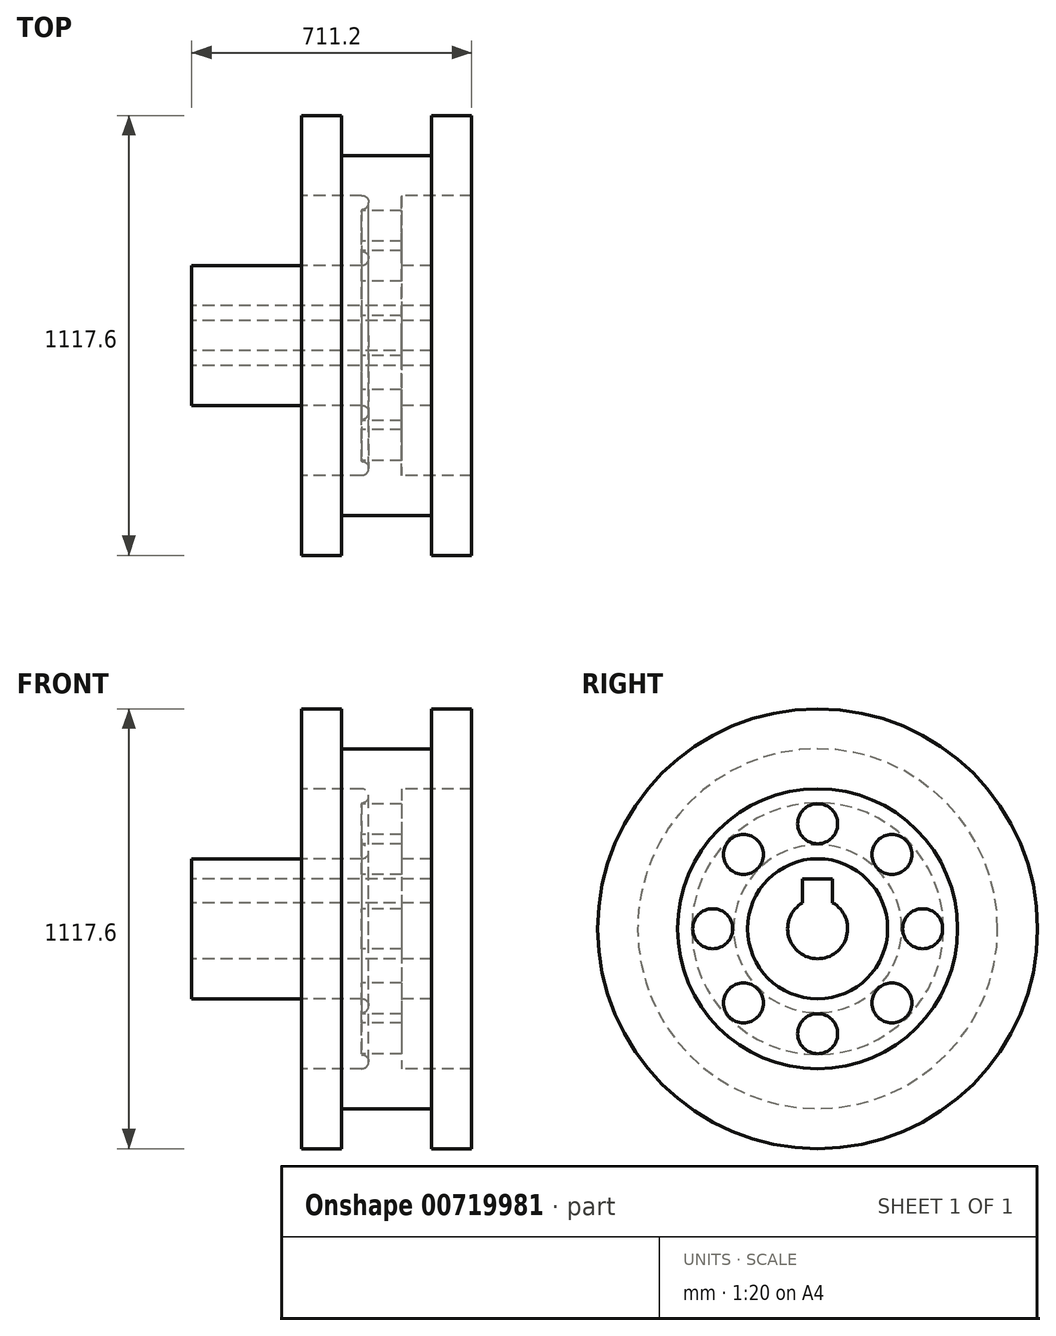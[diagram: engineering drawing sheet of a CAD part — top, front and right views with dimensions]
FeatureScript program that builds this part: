
annotation { "Feature Type Name" : "Feature", "Feature Type Description" : "" }
export const myFeature = defineFeature(function(context is Context, id is Id, definition is map)
    precondition{}
    {
        {
            var Q0;
            Q0=qCreatedBy(makeId("Front.planeOp"),FACE);
            var sketch = newSketch(context, id + "F0", { "sketchPlane" : qUnion([Q0])});
            skLineSegment(sketch, "E0", {"start": v(0, 0) * mm, "end": v(704.64, 0) * mm, "construction": true});
            skLineSegment(sketch, "E1", {"start": v(191.7, 0) * mm, "end": v(191.7, -76.2) * mm});
            skLineSegment(sketch, "E2", {"start": v(191.7, -76.2) * mm, "end": v(191.7, -177.8) * mm});
            skLineSegment(sketch, "E3", {"start": v(191.7, -76.2) * mm, "end": v(801.3, -76.2) * mm});
            skLineSegment(sketch, "E4", {"start": v(801.3, -76.2) * mm, "end": v(801.3, -177.8) * mm});
            skLineSegment(sketch, "E5", {"start": v(801.3, -177.8) * mm, "end": v(725.1, -177.8) * mm});
            skLineSegment(sketch, "E6", {"start": v(725.1, -177.8) * mm, "end": v(725.1, -355.6) * mm});
            skLineSegment(sketch, "E7", {"start": v(725.1, -355.6) * mm, "end": v(902.9, -355.6) * mm});
            skLineSegment(sketch, "E8", {"start": v(902.9, -355.6) * mm, "end": v(902.9, -558.8) * mm});
            skLineSegment(sketch, "E9", {"start": v(902.9, -558.8) * mm, "end": v(801.3, -558.8) * mm});
            skLineSegment(sketch, "E10", {"start": v(801.3, -558.8) * mm, "end": v(801.3, -457.2) * mm});
            skLineSegment(sketch, "E11", {"start": v(801.3, -457.2) * mm, "end": v(572.7, -457.2) * mm});
            skLineSegment(sketch, "E12", {"start": v(572.7, -457.2) * mm, "end": v(572.7, -558.8) * mm});
            skLineSegment(sketch, "E13", {"start": v(572.7, -558.8) * mm, "end": v(471.1, -558.8) * mm});
            skLineSegment(sketch, "E14", {"start": v(471.1, -558.8) * mm, "end": v(471.1, -355.6) * mm});
            skLineSegment(sketch, "E15", {"start": v(471.1, -355.6) * mm, "end": v(623.5, -355.6) * mm});
            skLineSegment(sketch, "E16", {"start": v(623.5, -177.8) * mm, "end": v(191.7, -177.8) * mm});
            skLineSegment(sketch, "E17", {"start": v(623.5, -266.7) * mm, "end": v(422.52, -266.7) * mm, "construction": true});
            skLineSegment(sketch, "E18", {"start": v(623.5, -177.8) * mm, "end": v(623.5, -213.4) * mm, "construction": true});
            skArc(sketch, "E19", {"start": v(623.5, -213.4) * mm, "mid": v(641.3, -195.6) * mm, "end": v(623.5, -177.8) * mm});
            skLineSegment(sketch, "E20", {"start": v(623.5, -355.6) * mm, "end": v(623.5, -320) * mm, "construction": true});
            skArc(sketch, "E21", {"start": v(623.5, -355.6) * mm, "mid": v(641.3, -337.8) * mm, "end": v(623.5, -320) * mm});
            skLineSegment(sketch, "E22.trimOffspring", {"start": v(623.5, -320) * mm, "end": v(623.5, -213.4) * mm});
            skSolve(sketch);
        }
        {
            var Q0;
            Q0=makeQuery(id+"F0.imprint","IMPRINT",FACE,{"disambiguationData":[TD([[makeQuery(id+"F0.imprint","IMPRINT",EDGE,{"derivedFrom":sQuery(id+"F0.wireOp",EDGE,"E2")}),1.0]])]});
            var Q1;
            Q1=sQuery(id+"F0.wireOp",EDGE,"E0");
            revolve(context, id + "F1", {"surfaceOperationType" : NewSurfaceOperationType.NEW, "entities" : qUnion([Q0]), "axis" : qUnion([Q1]), "revolveType" : RevolveType.FULL});
        }
        {
            var Q0;
            Q0=makeQuery(id+"F1.opRevolve","SWEPT_FACE",FACE,{"disambiguationData":[OSD([sQuery(id+"F0.wireOp",EDGE,"E2")])]});
            var sketch = newSketch(context, id + "F2", { "sketchPlane" : qUnion([Q0])});
            skLineSegment(sketch, "E23", {"start": v(0, 0) * mm, "end": v(582.75, 0) * mm, "construction": true});
            skLineSegment(sketch, "E24", {"start": v(0, 0) * mm, "end": v(-600.6, 0) * mm, "construction": true});
            skLineSegment(sketch, "E25", {"start": v(0, 0) * mm, "end": v(0, -510.8) * mm, "construction": true});
            skLineSegment(sketch, "E26", {"start": v(0, 0) * mm, "end": v(0, 561.94) * mm, "construction": true});
            skLineSegment(sketch, "E27.top", {"start": v(0, 127) * mm, "end": v(-38.1, 127) * mm});
            skLineSegment(sketch, "E27.right", {"start": v(-38.1, 0) * mm, "end": v(-38.1, 127) * mm});
            skLineSegment(sketch, "E28.top", {"start": v(0, 127) * mm, "end": v(38.1, 127) * mm});
            skLineSegment(sketch, "E28.right", {"start": v(38.1, 0) * mm, "end": v(38.1, 127) * mm});
            skCircle(sketch, "E29.cCircle", {"center": v(0, 0) * mm, "radius": 266.7 * mm, "construction": true});
            skLineSegment(sketch, "E29.0", {"start": v(266.7, 110.47) * mm, "end": v(266.7, -110.47) * mm});
            skLineSegment(sketch, "E29.1", {"start": v(266.7, -110.47) * mm, "end": v(110.47, -266.7) * mm});
            skLineSegment(sketch, "E29.2", {"start": v(110.47, -266.7) * mm, "end": v(-110.47, -266.7) * mm});
            skLineSegment(sketch, "E29.3", {"start": v(-110.47, -266.7) * mm, "end": v(-266.7, -110.47) * mm});
            skLineSegment(sketch, "E29.4", {"start": v(-266.7, -110.47) * mm, "end": v(-266.7, 110.47) * mm});
            skLineSegment(sketch, "E29.5", {"start": v(-266.7, 110.47) * mm, "end": v(-110.47, 266.7) * mm});
            skLineSegment(sketch, "E29.6", {"start": v(-110.47, 266.7) * mm, "end": v(110.47, 266.7) * mm});
            skLineSegment(sketch, "E29.7", {"start": v(110.47, 266.7) * mm, "end": v(266.7, 110.47) * mm});
            skPoint(sketch, "E29.0.midPoint", {"position": v(266.7, 0) * mm});
            skSolve(sketch);
        }
        {
            var Q0;
            {var subQ5=sQuery(id+"F2.wireOp",EDGE,"E27.top");Q0=makeQuery(id+"F2.imprint","IMPRINT",FACE,{"disambiguationData":[TD([[makeQuery(id+"F2.imprint","IMPRINT",EDGE,{"derivedFrom":subQ5}),1.0]])]});}
            extrude(context, id + "F3", {"entities" : qUnion([Q0]), "operationType" : NewBodyOperationType.REMOVE, "endBound" : BoundingType.THROUGH_ALL, "oppositeDirection" : true, "depth" : 25.4 * mm, "offsetDistance" : 25.4 * mm});
        }
        {
            var Q0;
            Q0=qCreatedBy(makeId("Right.planeOp"),FACE);
            var sketch = newSketch(context, id + "F4", { "sketchPlane" : qUnion([Q0])});
            skCircle(sketch, "E30.cCircle", {"center": v(0, 0) * mm, "radius": 266.7 * mm, "construction": true});
            skLineSegment(sketch, "E30.0", {"start": v(-266.7, -110.47) * mm, "end": v(-266.7, 110.47) * mm});
            skLineSegment(sketch, "E30.1", {"start": v(-266.7, 110.47) * mm, "end": v(-110.47, 266.7) * mm});
            skLineSegment(sketch, "E30.2", {"start": v(-110.47, 266.7) * mm, "end": v(110.47, 266.7) * mm});
            skLineSegment(sketch, "E30.3", {"start": v(110.47, 266.7) * mm, "end": v(266.7, 110.47) * mm});
            skLineSegment(sketch, "E30.4", {"start": v(266.7, 110.47) * mm, "end": v(266.7, -110.47) * mm});
            skLineSegment(sketch, "E30.5", {"start": v(266.7, -110.47) * mm, "end": v(110.47, -266.7) * mm});
            skLineSegment(sketch, "E30.6", {"start": v(110.47, -266.7) * mm, "end": v(-110.47, -266.7) * mm});
            skLineSegment(sketch, "E30.7", {"start": v(-110.47, -266.7) * mm, "end": v(-266.7, -110.47) * mm});
            skPoint(sketch, "E30.0.midPoint", {"position": v(-266.7, 0) * mm});
            skPoint(sketch, "E31", {"position": v(0, 266.7) * mm});
            skPoint(sketch, "E32", {"position": v(188.59, 188.59) * mm});
            skPoint(sketch, "E33", {"position": v(266.7, 0) * mm});
            skPoint(sketch, "E34", {"position": v(188.59, -188.59) * mm});
            skPoint(sketch, "E35", {"position": v(0, -266.7) * mm});
            skPoint(sketch, "E36", {"position": v(-188.59, -188.59) * mm});
            skPoint(sketch, "E37", {"position": v(-188.59, 188.59) * mm});
            skSolve(sketch);
        }
        {
            var Q0;
            Q0=sQuery(id+"F4.wireOp",VERTEX,"E31");
            var Q1;
            Q1=sQuery(id+"F4.wireOp",VERTEX,"E32");
            var Q2;
            Q2=sQuery(id+"F4.wireOp",VERTEX,"E33");
            var Q3;
            Q3=sQuery(id+"F4.wireOp",VERTEX,"E34");
            var Q4;
            Q4=sQuery(id+"F4.wireOp",VERTEX,"E35");
            var Q5;
            Q5=sQuery(id+"F4.wireOp",VERTEX,"E36");
            var Q6;
            Q6=sQuery(id+"F4.wireOp",VERTEX,"E30.0.midPoint");
            var Q7;
            Q7=sQuery(id+"F4.wireOp",VERTEX,"E37");
            var Q8;
            Q8=makeQuery(id+"F1.opRevolve","SWEPT_BODY",BODY,{"disambiguationData":[OSD([sQuery(id+"F0.wireOp",EDGE,"E2"),sQuery(id+"F0.wireOp",EDGE,"E3"),sQuery(id+"F0.wireOp",EDGE,"E4"),sQuery(id+"F0.wireOp",EDGE,"E5"),sQuery(id+"F0.wireOp",EDGE,"E6"),sQuery(id+"F0.wireOp",EDGE,"E7"),sQuery(id+"F0.wireOp",EDGE,"E8"),sQuery(id+"F0.wireOp",EDGE,"E9"),sQuery(id+"F0.wireOp",EDGE,"E10"),sQuery(id+"F0.wireOp",EDGE,"E11"),sQuery(id+"F0.wireOp",EDGE,"E12"),sQuery(id+"F0.wireOp",EDGE,"E13"),sQuery(id+"F0.wireOp",EDGE,"E14"),sQuery(id+"F0.wireOp",EDGE,"E15"),sQuery(id+"F0.wireOp",EDGE,"E16"),sQuery(id+"F0.wireOp",EDGE,"E19"),sQuery(id+"F0.wireOp",EDGE,"E21"),sQuery(id+"F0.wireOp",EDGE,"E22.trimOffspring")])]});
            hole(context, id + "F5", {"style" : HoleStyle.SIMPLE, "endStyle" : HoleEndStyle.THROUGH, "oppositeDirection" : true, "holeDiameter" : 101.6 * mm, "majorDiameter" : 6.35 * mm, "isTappedThrough" : true, "tappedDepth" : 12.7 * mm, "tapClearance" : 3, "locations" : qUnion([Q0, Q1, Q2, Q3, Q4, Q5, Q6, Q7]), "scope" : qUnion([Q8])});
        }
    });
